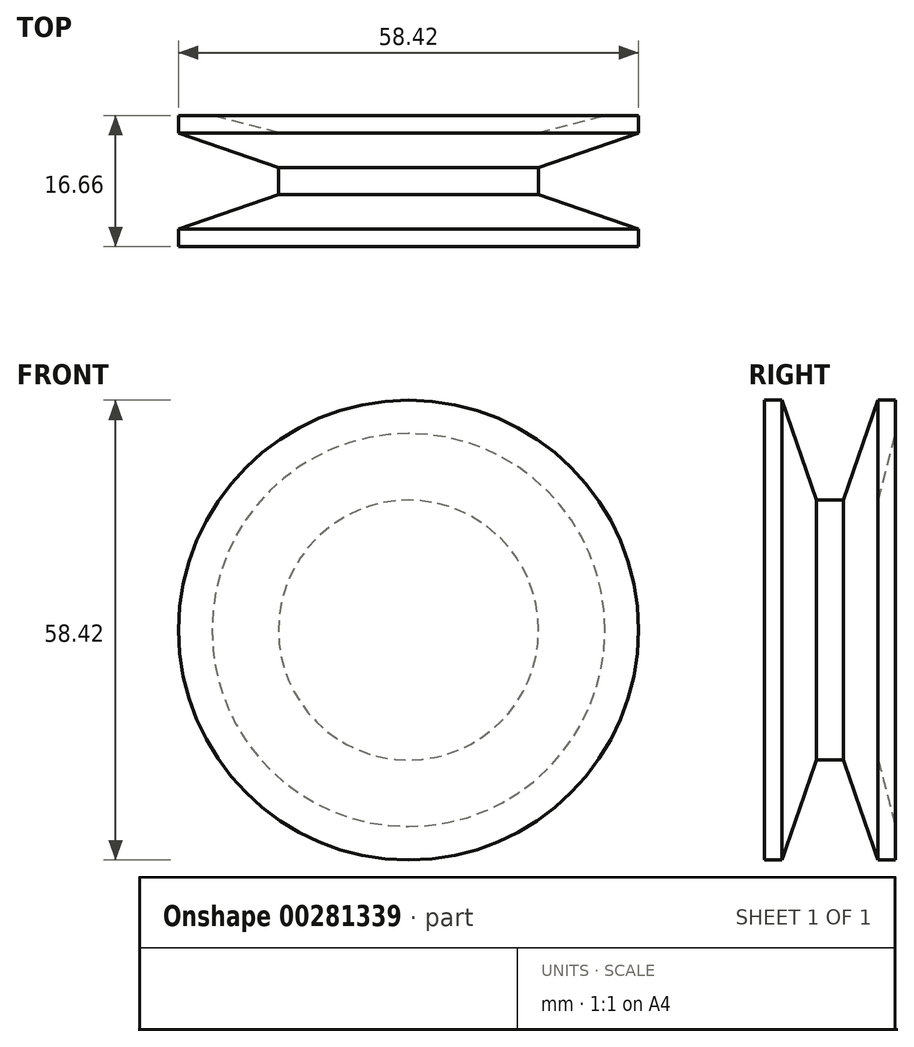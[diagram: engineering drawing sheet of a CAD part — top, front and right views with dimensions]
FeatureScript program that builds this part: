
annotation { "Feature Type Name" : "Feature", "Feature Type Description" : "" }
export const myFeature = defineFeature(function(context is Context, id is Id, definition is map)
    precondition{}
    {
        {
            var Q0;
            Q0=qCreatedBy(makeId("Right.planeOp"),FACE);
            var sketch = newSketch(context, id + "F0", { "sketchPlane" : qUnion([Q0])});
            skLineSegment(sketch, "E0", {"start": v(0, 16.51) * mm, "end": v(-1.72, 16.51) * mm});
            skLineSegment(sketch, "E1", {"start": v(-1.72, 16.5) * mm, "end": v(-6.1, 29.21) * mm});
            skLineSegment(sketch, "E2", {"start": v(-6.1, 29.21) * mm, "end": v(-8.33, 29.21) * mm});
            skLineSegment(sketch, "E3", {"start": v(-8.33, 29.21) * mm, "end": v(-8.33, 0) * mm});
            skLineSegment(sketch, "E4.MirrorCS", {"start": v(0, 16.51) * mm, "end": v(1.72, 16.51) * mm});
            skLineSegment(sketch, "E5.MirrorCS", {"start": v(1.72, 16.5) * mm, "end": v(6.1, 29.21) * mm});
            skLineSegment(sketch, "E6.MirrorCS", {"start": v(6.1, 29.21) * mm, "end": v(8.33, 29.21) * mm});
            skLineSegment(sketch, "E7", {"start": v(-8.33, 0) * mm, "end": v(6.14, 0) * mm});
            skLineSegment(sketch, "E8", {"start": v(8.33, 29.21) * mm, "end": v(8.33, 24.96) * mm});
            skLineSegment(sketch, "E9", {"start": v(8.33, 24.96) * mm, "end": v(6.14, 16.51) * mm});
            skLineSegment(sketch, "E10", {"start": v(6.14, 16.51) * mm, "end": v(6.14, 0) * mm});
            skPoint(sketch, "E11.orphan", {"position": v(8.33, 0) * mm});
            skSolve(sketch);
        }
        {
            var Q0;
            Q0 = qSketchRegion(id + "F0", true);
            var Q1;
            Q1=sQuery(id+"F0.wireOp",EDGE,"E7");
            revolve(context, id + "F1", {"entities" : qUnion([Q0]), "axis" : qUnion([Q1]), "revolveType" : RevolveType.FULL});
        }
    });
